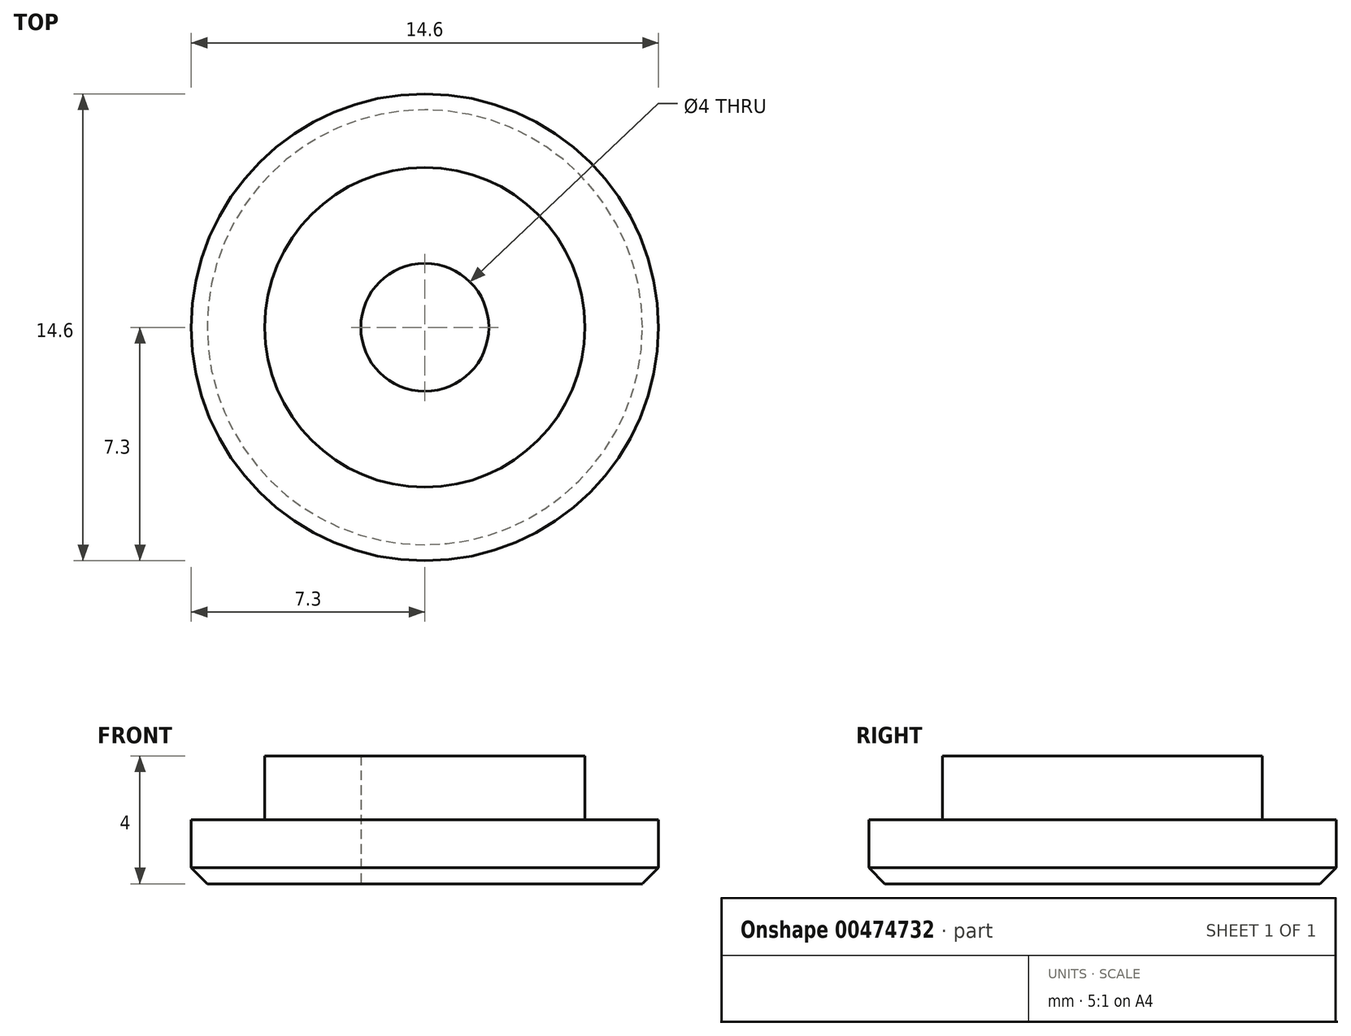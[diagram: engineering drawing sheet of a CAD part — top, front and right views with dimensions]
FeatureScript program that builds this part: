
annotation { "Feature Type Name" : "Feature", "Feature Type Description" : "" }
export const myFeature = defineFeature(function(context is Context, id is Id, definition is map)
    precondition{}
    {
        {
            var Q0;
            Q0=qCreatedBy(makeId("Top.planeOp"),FACE);
            var sketch = newSketch(context, id + "F0", { "sketchPlane" : qUnion([Q0])});
            skCircle(sketch, "E0", {"center": v(0, 0) * mm, "radius": 7.3 * mm});
            skSolve(sketch);
        }
        {
            var Q0;
            Q0 = qSketchRegion(id + "F0", true);
            extrude(context, id + "F1", {"entities" : qUnion([Q0]), "depth" : 2 * mm, "offsetDistance" : 25 * mm});
        }
        {
            var Q0;
            Q0=makeQuery(id+"F1.opExtrude","CAP_FACE",FACE,{"disambiguationData":[OSD([sQuery(id+"F0.wireOp",EDGE,"E0")])],"isStart":false});
            var sketch = newSketch(context, id + "F2", { "sketchPlane" : qUnion([Q0])});
            skCircle(sketch, "E1", {"center": v(0, 0) * mm, "radius": 5 * mm});
            skSolve(sketch);
        }
        {
            var Q0;
            Q0 = qSketchRegion(id + "F2", true);
            extrude(context, id + "F3", {"entities" : qUnion([Q0]), "operationType" : NewBodyOperationType.ADD, "depth" : 2 * mm, "offsetDistance" : 25 * mm});
        }
        {
            var Q0;
            Q0=makeQuery(id+"F1.opExtrude","CAP_EDGE",EDGE,{"disambiguationData":[OSD([sQuery(id+"F0.wireOp",EDGE,"E0")])],"isStart":true});
            chamfer(context, id + "F4", {"entities" : qUnion([Q0]), "width" : 0.5 * mm, "tangentPropagation" : true});
        }
        {
            var Q0;
            Q0=makeQuery(id+"F1.opExtrude","CAP_FACE",FACE,{"disambiguationData":[OSD([sQuery(id+"F0.wireOp",EDGE,"E0")])],"isStart":true});
            var sketch = newSketch(context, id + "F5", { "sketchPlane" : qUnion([Q0])});
            skCircle(sketch, "E2", {"center": v(0, 0) * mm, "radius": 2 * mm});
            skSolve(sketch);
        }
        {
            var Q0;
            Q0 = qSketchRegion(id + "F5", true);
            extrude(context, id + "F6", {"entities" : qUnion([Q0]), "operationType" : NewBodyOperationType.REMOVE, "endBound" : BoundingType.THROUGH_ALL, "oppositeDirection" : true, "depth" : 25 * mm, "offsetDistance" : 25 * mm});
        }
    });
